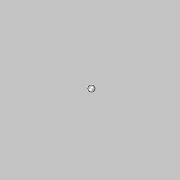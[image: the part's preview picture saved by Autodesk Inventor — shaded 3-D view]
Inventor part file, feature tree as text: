
AUTODESK INVENTOR PART (.ipt)
format: ipt  version: 2017 (Build 210142000, 142)  size: 107,520 bytes
history: native  units: mm
features: other x10, sketch x3, sweep x1, extrude x1, pattern_circular x1, projected_geometry x1
ambient origin geometry x7: Origin, YZ Plane, XZ Plane, X Axis, Y Axis, Z Axis, Center Point
bodies: Solid1 (feature_tree), Solid2 (feature_tree)
feature tree (17):
  other  "Table"
  other  "CableLadderBendKHJZP-150"
  other  "CableLadderBendKHJZP-200"
  other  "CableLadderBendKHJZP-300"
  other  "CableLadderBendKHJZP-400"
  other  "CableLadderBendKHJZP-500"
  other  "CableLadderBendKHJZP-600"
  other  "CableLadderBendKHJZP-800"
  other  "CableLadderBendKHJZP-1000"
  sweep  "Sweep1"
  extrude  "Extrusion2"  Depth=18.0mm
  pattern_circular  "Circular Pattern1"  Count=300  [1 undecoded]
  other  "XY Ground Plane"
  sketch  "Sketch4"  dims[d0=55.0mm d1=18.0mm]
  sketch  "Sketch5"  dims[d5=30.0mm d6=18.0mm d7=3000.0mm d8=0.0mm]
  sketch  "Sketch6"  dims[d14=268.0mm d16=400.0mm d17=0.0mm d18=0.0mm d20=50.0mm d21=90.0deg d24=0.0mm]
  projected_geometry  "Projected Loop1"
note: 1 required parameter value undecoded (feature->parameter linkage not recoverable at this tier; creation-order binding heuristic only, values carry confidence <= 0.55)
